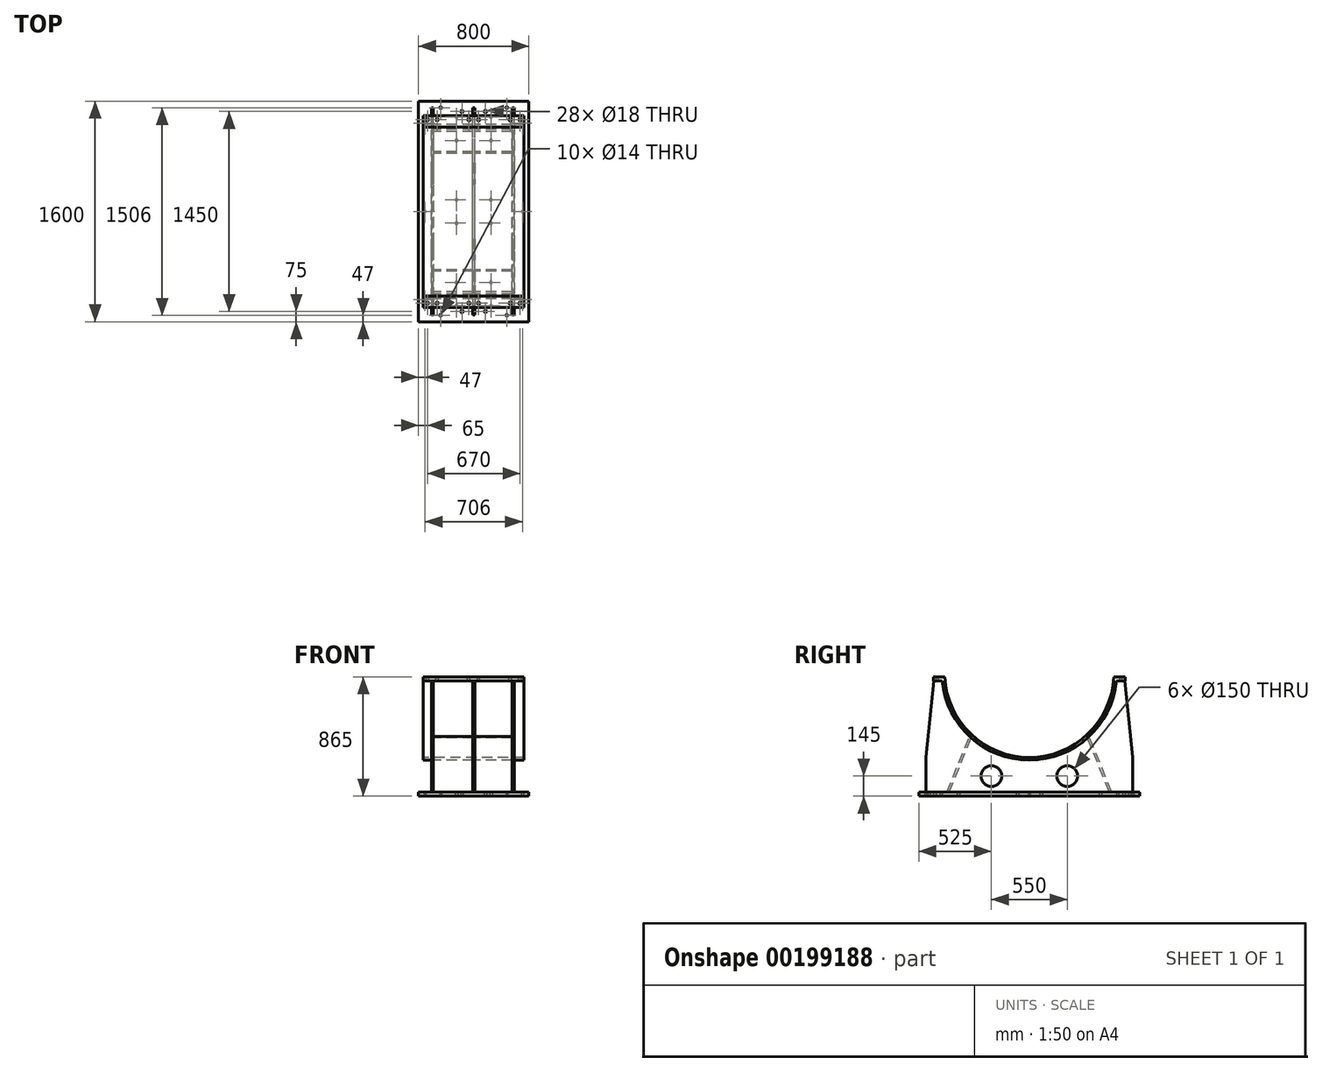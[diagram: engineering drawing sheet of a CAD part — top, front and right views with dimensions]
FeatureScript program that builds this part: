
annotation { "Feature Type Name" : "Feature", "Feature Type Description" : "" }
export const myFeature = defineFeature(function(context is Context, id is Id, definition is map)
    precondition{}
    {
        {
            var Q0;
            Q0=qCreatedBy(makeId("Right.planeOp"),FACE);
            var sketch = newSketch(context, id + "F0", { "sketchPlane" : qUnion([Q0])});
            skArc(sketch, "E0", {"start": v(-613.37, -30) * mm, "mid": v(0, -614.1) * mm, "end": v(613.37, -30) * mm});
            skArc(sketch, "E1", {"start": v(-633.39, -30) * mm, "mid": v(0, -634.1) * mm, "end": v(633.39, -30) * mm});
            skLineSegment(sketch, "E2", {"start": v(-634.1, 0) * mm, "end": v(634.1, 0) * mm, "construction": true});
            skLineSegment(sketch, "E3", {"start": v(-633.39, -30) * mm, "end": v(633.39, -30) * mm, "construction": true});
            skLineSegment(sketch, "E4", {"start": v(-633.39, -30) * mm, "end": v(-613.37, -30) * mm});
            skLineSegment(sketch, "E5", {"start": v(613.37, -30) * mm, "end": v(633.39, -30) * mm});
            skSolve(sketch);
        }
        {
            var Q0;
            Q0=makeQuery(id+"F0.imprint","IMPRINT",FACE,{"disambiguationData":[TD([[makeQuery(id+"F0.imprint","IMPRINT",EDGE,{"derivedFrom":sQuery(id+"F0.wireOp",EDGE,"E0")}),-1.0]])]});
            extrude(context, id + "F1", {"entities" : qUnion([Q0]), "endBound" : BoundingType.SYMMETRIC, "depth" : 730 * mm});
        }
        {
            var Q0;
            Q0=makeQuery(id+"F1.opExtrude","SWEPT_FACE",FACE,{"disambiguationData":[OSD([sQuery(id+"F0.wireOp",EDGE,"E5")])]});
            var sketch = newSketch(context, id + "F2", { "sketchPlane" : qUnion([Q0])});
            skLineSegment(sketch, "E6.bottom", {"start": v(-365, 613.37) * mm, "end": v(365, 613.37) * mm});
            skLineSegment(sketch, "E6.top", {"start": v(-365, 695.5) * mm, "end": v(365, 695.5) * mm});
            skLineSegment(sketch, "E6.left", {"start": v(-365, 613.37) * mm, "end": v(-365, 695.5) * mm});
            skLineSegment(sketch, "E6.right", {"start": v(365, 613.37) * mm, "end": v(365, 695.5) * mm});
            skLineSegment(sketch, "E7", {"start": v(-365, 0) * mm, "end": v(365, 0) * mm, "construction": true});
            skLineSegment(sketch, "E8.MirrorCS", {"start": v(-365, -613.37) * mm, "end": v(365, -613.37) * mm});
            skLineSegment(sketch, "E9.MirrorCS", {"start": v(-365, -613.37) * mm, "end": v(-365, -695.5) * mm});
            skLineSegment(sketch, "E10.MirrorCS", {"start": v(-365, -695.5) * mm, "end": v(365, -695.5) * mm});
            skLineSegment(sketch, "E11.MirrorCS", {"start": v(365, -613.37) * mm, "end": v(365, -695.5) * mm});
            skSolve(sketch);
        }
        {
            var Q0;
            Q0 = qSketchRegion(id + "F2", true);
            extrude(context, id + "F3", {"entities" : qUnion([Q0]), "operationType" : NewBodyOperationType.ADD, "oppositeDirection" : true, "depth" : 30 * mm});
        }
        {
            var Q0;
            Q0=makeQuery(id+"F3.boolean.opBoolean","MERGE",FACE,{"derivedFrom":[makeQuery(id+"F1.opExtrude","SWEPT_FACE",FACE,{"disambiguationData":[OSD([sQuery(id+"F0.wireOp",EDGE,"E5")])]}),makeQuery(id+"F3.opExtrude","CAP_FACE",FACE,{"disambiguationData":[OSD([sQuery(id+"F2.wireOp",EDGE,"E6.bottom"),sQuery(id+"F2.wireOp",EDGE,"E6.top"),sQuery(id+"F2.wireOp",EDGE,"E6.left"),sQuery(id+"F2.wireOp",EDGE,"E6.right")])],"isStart":true})]});
            var sketch = newSketch(context, id + "F4", { "sketchPlane" : qUnion([Q0])});
            skLineSegment(sketch, "E12", {"start": v(-365, 665.5) * mm, "end": v(365, 665.5) * mm, "construction": true});
            skCircle(sketch, "E13", {"center": v(-335, 665.5) * mm, "radius": 9 * mm});
            skCircle(sketch, "E14", {"center": v(-265, 665.5) * mm, "radius": 9 * mm});
            skCircle(sketch, "E15", {"center": v(-35, 665.5) * mm, "radius": 9 * mm});
            skCircle(sketch, "E16", {"center": v(35, 665.5) * mm, "radius": 9 * mm});
            skCircle(sketch, "E17", {"center": v(265, 665.5) * mm, "radius": 9 * mm});
            skCircle(sketch, "E18", {"center": v(335, 665.5) * mm, "radius": 9 * mm});
            skLineSegment(sketch, "E19", {"start": v(0, 0) * mm, "end": v(0, 665.5) * mm, "construction": true});
            skLineSegment(sketch, "E20", {"start": v(-365, 0) * mm, "end": v(365, 0) * mm, "construction": true});
            skCircle(sketch, "E21.MirrorC", {"center": v(-265, -665.5) * mm, "radius": 9 * mm});
            skCircle(sketch, "E22.MirrorC", {"center": v(-335, -665.5) * mm, "radius": 9 * mm});
            skCircle(sketch, "E23.MirrorC", {"center": v(-35, -665.5) * mm, "radius": 9 * mm});
            skCircle(sketch, "E24.MirrorC", {"center": v(35, -665.5) * mm, "radius": 9 * mm});
            skCircle(sketch, "E25.MirrorC", {"center": v(265, -665.5) * mm, "radius": 9 * mm});
            skCircle(sketch, "E26.MirrorC", {"center": v(335, -665.5) * mm, "radius": 9 * mm});
            skSolve(sketch);
        }
        {
            var Q0;
            Q0 = qSketchRegion(id + "F4", true);
            extrude(context, id + "F5", {"entities" : qUnion([Q0]), "operationType" : NewBodyOperationType.REMOVE, "endBound" : BoundingType.THROUGH_ALL, "oppositeDirection" : true, "depth" : 25 * mm});
        }
        {
            var Q0;
            Q0=makeQuery(id+"F3.boolean.opBoolean","MERGE",FACE,{"derivedFrom":[makeQuery(id+"F1.opExtrude","CAP_FACE",FACE,{"disambiguationData":[OSD([sQuery(id+"F0.wireOp",EDGE,"E0"),sQuery(id+"F0.wireOp",EDGE,"E1"),sQuery(id+"F0.wireOp",EDGE,"E4"),sQuery(id+"F0.wireOp",EDGE,"E5")])],"isStart":true}),makeQuery(id+"F3.opExtrude","SWEPT_FACE",FACE,{"disambiguationData":[OSD([sQuery(id+"F2.wireOp",EDGE,"E6.left")])]}),makeQuery(id+"F3.opExtrude","SWEPT_FACE",FACE,{"disambiguationData":[OSD([sQuery(id+"F2.wireOp",EDGE,"E9.MirrorCS")])]})]});
            cPlane(context, id + "F6", {"entities" : qUnion([Q0]), "cplaneType" : CPlaneType.OFFSET, "offset" : 73 * mm, "oppositeDirection" : true, "width" : 150 * mm, "height" : 150 * mm});
        }
        {
            var Q0;
            Q0=qCreatedBy(id+"F6.planeOp",FACE);
            var sketch = newSketch(context, id + "F7", { "sketchPlane" : qUnion([Q0])});
            skLineSegment(sketch, "E27", {"start": v(0, 0) * mm, "end": v(0, -865) * mm, "construction": true});
            skLineSegment(sketch, "E28", {"start": v(750, -865) * mm, "end": v(-750, -865) * mm});
            skLineSegment(sketch, "E29", {"start": v(-750, -865) * mm, "end": v(-750, -612) * mm});
            skLineSegment(sketch, "E30", {"start": v(-750, -612) * mm, "end": v(-692, -60) * mm});
            skLineSegment(sketch, "E31.0", {"start": v(-631.25, -60) * mm, "end": v(-692, -60) * mm});
            skPoint(sketch, "E32.orphan", {"position": v(-695.5, -60) * mm});
            skArc(sketch, "E33.0", {"start": v(631.25, -60) * mm, "mid": v(0, -634.1) * mm, "end": v(-631.25, -60) * mm});
            skLineSegment(sketch, "E34.MirrorCS", {"start": v(631.25, -60) * mm, "end": v(692, -60) * mm});
            skLineSegment(sketch, "E35.MirrorCS", {"start": v(750, -612) * mm, "end": v(692, -60) * mm});
            skLineSegment(sketch, "E36.MirrorCS", {"start": v(750, -865) * mm, "end": v(750, -612) * mm});
            skCircle(sketch, "E37", {"center": v(-275, -750) * mm, "radius": 75 * mm});
            skCircle(sketch, "E38.MirrorC", {"center": v(275, -750) * mm, "radius": 75 * mm});
            skSolve(sketch);
        }
        {
            var Q0;
            Q0=makeQuery(id+"F7.imprint","IMPRINT",FACE,{"disambiguationData":[TD([[makeQuery(id+"F7.imprint","IMPRINT",EDGE,{"derivedFrom":sQuery(id+"F7.wireOp",EDGE,"E28")}),-1.0]])]});
            extrude(context, id + "F8", {"entities" : qUnion([Q0]), "operationType" : NewBodyOperationType.ADD, "depth" : 15 * mm});
        }
        {
            var Q0;
            Q0=makeQuery(id+"F8.opExtrude","CAP_FACE",FACE,{"disambiguationData":[OSD([sQuery(id+"F7.wireOp",EDGE,"E28"),sQuery(id+"F7.wireOp",EDGE,"E29"),sQuery(id+"F7.wireOp",EDGE,"E30"),sQuery(id+"F7.wireOp",EDGE,"E31.0"),sQuery(id+"F7.wireOp",EDGE,"E33.0"),sQuery(id+"F7.wireOp",EDGE,"E34.MirrorCS"),sQuery(id+"F7.wireOp",EDGE,"E35.MirrorCS"),sQuery(id+"F7.wireOp",EDGE,"E36.MirrorCS"),sQuery(id+"F7.wireOp",EDGE,"E37"),sQuery(id+"F7.wireOp",EDGE,"E38.MirrorC")])],"isStart":true});
            cPlane(context, id + "F9", {"entities" : qUnion([Q0]), "cplaneType" : CPlaneType.OFFSET, "offset" : 300 * mm, "width" : 150 * mm, "height" : 150 * mm});
        }
        {
            var Q0;
            Q0=qCreatedBy(id+"F9.planeOp",FACE);
            var sketch = newSketch(context, id + "F10", { "sketchPlane" : qUnion([Q0])});
            skLineSegment(sketch, "E39.0", {"start": v(631.25, -60) * mm, "end": v(692, -60) * mm});
            skLineSegment(sketch, "E40.0", {"start": v(750, -612) * mm, "end": v(692, -60) * mm});
            skArc(sketch, "E41.0", {"start": v(-631.25, -60) * mm, "mid": v(0, -634.1) * mm, "end": v(631.25, -60) * mm});
            skLineSegment(sketch, "E42.0", {"start": v(750, -865) * mm, "end": v(750, -612) * mm});
            skLineSegment(sketch, "E43.0", {"start": v(-750, -865) * mm, "end": v(750, -865) * mm});
            skCircle(sketch, "E44.0", {"center": v(275, -750) * mm, "radius": 75 * mm});
            skCircle(sketch, "E45.0", {"center": v(-275, -750) * mm, "radius": 75 * mm});
            skLineSegment(sketch, "E46.0", {"start": v(-750, -865) * mm, "end": v(-750, -612) * mm});
            skLineSegment(sketch, "E47.0", {"start": v(-750, -612) * mm, "end": v(-692, -60) * mm});
            skLineSegment(sketch, "E48.0", {"start": v(-631.25, -60) * mm, "end": v(-692, -60) * mm});
            skSolve(sketch);
        }
        {
            var Q0;
            Q0=makeQuery(id+"F10.imprint","IMPRINT",FACE,{"disambiguationData":[TD([[makeQuery(id+"F10.imprint","IMPRINT",EDGE,{"derivedFrom":sQuery(id+"F10.wireOp",EDGE,"E39.0")}),-1.0]])]});
            extrude(context, id + "F11", {"entities" : qUnion([Q0]), "operationType" : NewBodyOperationType.ADD, "oppositeDirection" : true, "depth" : 15 * mm});
        }
        {
            var Q0;
            Q0=makeQuery(id+"F11.opExtrude","CAP_FACE",FACE,{"disambiguationData":[OSD([sQuery(id+"F10.wireOp",EDGE,"E39.0"),sQuery(id+"F10.wireOp",EDGE,"E40.0"),sQuery(id+"F10.wireOp",EDGE,"E41.0"),sQuery(id+"F10.wireOp",EDGE,"E42.0"),sQuery(id+"F10.wireOp",EDGE,"E43.0"),sQuery(id+"F10.wireOp",EDGE,"E44.0"),sQuery(id+"F10.wireOp",EDGE,"E45.0"),sQuery(id+"F10.wireOp",EDGE,"E46.0"),sQuery(id+"F10.wireOp",EDGE,"E47.0"),sQuery(id+"F10.wireOp",EDGE,"E48.0")])],"isStart":false});
            cPlane(context, id + "F12", {"entities" : qUnion([Q0]), "cplaneType" : CPlaneType.OFFSET, "offset" : 300 * mm, "oppositeDirection" : true, "width" : 150 * mm, "height" : 150 * mm});
        }
        {
            var Q0;
            Q0=qCreatedBy(id+"F12.planeOp",FACE);
            var sketch = newSketch(context, id + "F13", { "sketchPlane" : qUnion([Q0])});
            skLineSegment(sketch, "E49.0", {"start": v(750, -612) * mm, "end": v(692, -60) * mm});
            skLineSegment(sketch, "E50.0", {"start": v(750, -865) * mm, "end": v(750, -612) * mm});
            skLineSegment(sketch, "E51.0", {"start": v(750, -865) * mm, "end": v(-750, -865) * mm});
            skCircle(sketch, "E52.0", {"center": v(275, -750) * mm, "radius": 75 * mm});
            skCircle(sketch, "E53.0", {"center": v(-275, -750) * mm, "radius": 75 * mm});
            skLineSegment(sketch, "E54.0", {"start": v(-750, -865) * mm, "end": v(-750, -612) * mm});
            skLineSegment(sketch, "E55.0", {"start": v(-750, -612) * mm, "end": v(-692, -60) * mm});
            skArc(sketch, "E56.0", {"start": v(631.25, -60) * mm, "mid": v(0, -634.1) * mm, "end": v(-631.25, -60) * mm});
            skLineSegment(sketch, "E57.0", {"start": v(-631.25, -60) * mm, "end": v(-692, -60) * mm});
            skLineSegment(sketch, "E58.0", {"start": v(631.25, -60) * mm, "end": v(692, -60) * mm});
            skSolve(sketch);
        }
        {
            var Q0;
            Q0=makeQuery(id+"F13.imprint","IMPRINT",FACE,{"disambiguationData":[TD([[makeQuery(id+"F13.imprint","IMPRINT",EDGE,{"derivedFrom":sQuery(id+"F13.wireOp",EDGE,"E49.0")}),1.0]])]});
            extrude(context, id + "F14", {"entities" : qUnion([Q0]), "operationType" : NewBodyOperationType.ADD, "depth" : 15 * mm});
        }
        {
            var Q0;
            Q0=makeQuery(id+"F8.opExtrude","SWEPT_FACE",FACE,{"disambiguationData":[OSD([sQuery(id+"F7.wireOp",EDGE,"E28")])]});
            var sketch = newSketch(context, id + "F15", { "sketchPlane" : qUnion([Q0])});
            skLineSegment(sketch, "E59.bottom", {"start": v(-400, 800) * mm, "end": v(400, 800) * mm});
            skLineSegment(sketch, "E59.top", {"start": v(-400, -800) * mm, "end": v(400, -800) * mm});
            skLineSegment(sketch, "E59.left", {"start": v(-400, 800) * mm, "end": v(-400, -800) * mm});
            skLineSegment(sketch, "E59.right", {"start": v(400, 800) * mm, "end": v(400, -800) * mm});
            skLineSegment(sketch, "E60", {"start": v(0, 0) * mm, "end": v(400, 0) * mm, "construction": true});
            skLineSegment(sketch, "E61", {"start": v(0, 800) * mm, "end": v(0, 0) * mm, "construction": true});
            skSolve(sketch);
        }
        {
            var Q0;
            Q0 = qSketchRegion(id + "F15", true);
            extrude(context, id + "F16", {"entities" : qUnion([Q0]), "operationType" : NewBodyOperationType.ADD, "depth" : 30 * mm});
        }
        {
            var Q0;
            Q0=makeQuery(id+"F8.opExtrude","CAP_FACE",FACE,{"disambiguationData":[OSD([sQuery(id+"F7.wireOp",EDGE,"E28"),sQuery(id+"F7.wireOp",EDGE,"E29"),sQuery(id+"F7.wireOp",EDGE,"E30"),sQuery(id+"F7.wireOp",EDGE,"E31.0"),sQuery(id+"F7.wireOp",EDGE,"E33.0"),sQuery(id+"F7.wireOp",EDGE,"E34.MirrorCS"),sQuery(id+"F7.wireOp",EDGE,"E35.MirrorCS"),sQuery(id+"F7.wireOp",EDGE,"E36.MirrorCS"),sQuery(id+"F7.wireOp",EDGE,"E37"),sQuery(id+"F7.wireOp",EDGE,"E38.MirrorC")])],"isStart":false});
            var sketch = newSketch(context, id + "F17", { "sketchPlane" : qUnion([Q0])});
            skLineSegment(sketch, "E62", {"start": v(-596.7, -865) * mm, "end": v(-434, -462.3) * mm});
            skLineSegment(sketch, "E63", {"start": v(-580.52, -865) * mm, "end": v(-422.19, -473.12) * mm});
            skLineSegment(sketch, "E64", {"start": v(0, -865) * mm, "end": v(0, -634.1) * mm, "construction": true});
            skArc(sketch, "E65.0", {"start": v(631.25, -60) * mm, "mid": v(426.64, -469.11) * mm, "end": v(0, -634.1) * mm});
            skLineSegment(sketch, "E66.0", {"start": v(800, -865) * mm, "end": v(0, -865) * mm});
            skPoint(sketch, "E67.orphan", {"position": v(-631.25, -60) * mm});
            skArc(sketch, "E68.trimOffspring", {"start": v(-422.19, -473.12) * mm, "mid": v(-428.13, -467.75) * mm, "end": v(-434, -462.3) * mm});
            skLineSegment(sketch, "E69.trimOffspring", {"start": v(-580.52, -865) * mm, "end": v(-596.7, -865) * mm});
            skPoint(sketch, "E70.orphan", {"position": v(-800, -865) * mm});
            skLineSegment(sketch, "E71.MirrorCS", {"start": v(580.52, -865) * mm, "end": v(422.19, -473.12) * mm});
            skLineSegment(sketch, "E72.MirrorCS", {"start": v(596.7, -865) * mm, "end": v(434, -462.3) * mm});
            skArc(sketch, "E73.MirrorCS", {"start": v(422.19, -473.12) * mm, "mid": v(428.13, -467.75) * mm, "end": v(434, -462.3) * mm});
            skLineSegment(sketch, "E74.MirrorCS", {"start": v(580.52, -865) * mm, "end": v(596.7, -865) * mm});
            skSolve(sketch);
        }
        {
            var Q0;
            Q0 = qSketchRegion(id + "F17", true);
            var Q1;
            Q1=makeQuery(id+"F14.opExtrude","CAP_FACE",FACE,{"disambiguationData":[OSD([sQuery(id+"F13.wireOp",EDGE,"E49.0"),sQuery(id+"F13.wireOp",EDGE,"E50.0"),sQuery(id+"F13.wireOp",EDGE,"E51.0"),sQuery(id+"F13.wireOp",EDGE,"E52.0"),sQuery(id+"F13.wireOp",EDGE,"E53.0"),sQuery(id+"F13.wireOp",EDGE,"E54.0"),sQuery(id+"F13.wireOp",EDGE,"E55.0"),sQuery(id+"F13.wireOp",EDGE,"E56.0"),sQuery(id+"F13.wireOp",EDGE,"E57.0"),sQuery(id+"F13.wireOp",EDGE,"E58.0")])],"isStart":true});
            extrude(context, id + "F18", {"entities" : qUnion([Q0]), "operationType" : NewBodyOperationType.ADD, "endBound" : BoundingType.UP_TO_SURFACE, "oppositeDirection" : true, "endBoundEntityFace" : qUnion([Q1]), "depth" : 25 * mm});
        }
        {
            var Q0;
            Q0=makeQuery(id+"F16.opExtrude","CAP_FACE",FACE,{"disambiguationData":[OSD([sQuery(id+"F15.wireOp",EDGE,"E59.bottom"),sQuery(id+"F15.wireOp",EDGE,"E59.top"),sQuery(id+"F15.wireOp",EDGE,"E59.left"),sQuery(id+"F15.wireOp",EDGE,"E59.right")])],"isStart":false});
            var sketch = newSketch(context, id + "F19", { "sketchPlane" : qUnion([Q0])});
            skLineSegment(sketch, "E75", {"start": v(-400, 753) * mm, "end": v(400, 753) * mm, "construction": true});
            skLineSegment(sketch, "E76", {"start": v(-400, 725) * mm, "end": v(400, 725) * mm, "construction": true});
            skLineSegment(sketch, "E77", {"start": v(-400, 640) * mm, "end": v(400, 640) * mm, "construction": true});
            skLineSegment(sketch, "E78", {"start": v(-400, 0) * mm, "end": v(400, 0) * mm, "construction": true});
            skCircle(sketch, "E79", {"center": v(-353, 0) * mm, "radius": 7 * mm});
            skCircle(sketch, "E80", {"center": v(353, 0) * mm, "radius": 7 * mm});
            skCircle(sketch, "E81", {"center": v(-353, 640) * mm, "radius": 7 * mm});
            skLineSegment(sketch, "E82", {"start": v(0, 800) * mm, "end": v(0, 0) * mm, "construction": true});
            skCircle(sketch, "E83", {"center": v(-240, 753) * mm, "radius": 7 * mm});
            skCircle(sketch, "E84", {"center": v(-85, 725) * mm, "radius": 9 * mm});
            skCircle(sketch, "E85.MirrorC", {"center": v(85, 725) * mm, "radius": 9 * mm});
            skCircle(sketch, "E86.MirrorC", {"center": v(240, 753) * mm, "radius": 7 * mm});
            skCircle(sketch, "E87.MirrorC", {"center": v(353, 640) * mm, "radius": 7 * mm});
            skCircle(sketch, "E88.MirrorC", {"center": v(-353, -640) * mm, "radius": 7 * mm});
            skCircle(sketch, "E89.MirrorC", {"center": v(-240, -753) * mm, "radius": 7 * mm});
            skCircle(sketch, "E90.MirrorC", {"center": v(-85, -725) * mm, "radius": 9 * mm});
            skCircle(sketch, "E91.MirrorC", {"center": v(85, -725) * mm, "radius": 9 * mm});
            skCircle(sketch, "E92.MirrorC", {"center": v(353, -640) * mm, "radius": 7 * mm});
            skCircle(sketch, "E93.MirrorC", {"center": v(240, -753) * mm, "radius": 7 * mm});
            skSolve(sketch);
        }
        {
            var Q0;
            Q0 = qSketchRegion(id + "F19", true);
            extrude(context, id + "F20", {"entities" : qUnion([Q0]), "operationType" : NewBodyOperationType.REMOVE, "oppositeDirection" : true, "depth" : 31 * mm});
        }
        {
            var Q0;
            Q0=makeQuery(id+"F16.opExtrude","CAP_FACE",FACE,{"disambiguationData":[OSD([sQuery(id+"F15.wireOp",EDGE,"E59.bottom"),sQuery(id+"F15.wireOp",EDGE,"E59.top"),sQuery(id+"F15.wireOp",EDGE,"E59.left"),sQuery(id+"F15.wireOp",EDGE,"E59.right")])],"isStart":false});
            var sketch = newSketch(context, id + "F21", { "sketchPlane" : qUnion([Q0])});
            skLineSegment(sketch, "E94", {"start": v(400, 700) * mm, "end": v(-400, 700) * mm, "construction": true});
            skLineSegment(sketch, "E95", {"start": v(-400, 500) * mm, "end": v(400, 500) * mm, "construction": true});
            skLineSegment(sketch, "E96", {"start": v(-400, 100) * mm, "end": v(400, 100) * mm, "construction": true});
            skLineSegment(sketch, "E97", {"start": v(-400, -100) * mm, "end": v(400, -100) * mm, "construction": true});
            skLineSegment(sketch, "E98", {"start": v(-400, -400) * mm, "end": v(400, -400) * mm, "construction": true});
            skLineSegment(sketch, "E99", {"start": v(-400, -600) * mm, "end": v(400, -600) * mm, "construction": true});
            skLineSegment(sketch, "E100", {"start": v(-400, 0) * mm, "end": v(400, 0) * mm, "construction": true});
            skLineSegment(sketch, "E101", {"start": v(-400, 600) * mm, "end": v(400, 600) * mm, "construction": true});
            skLineSegment(sketch, "E102", {"start": v(0, 800) * mm, "end": v(0, 0) * mm, "construction": true});
            skCircle(sketch, "E103", {"center": v(-125, 685) * mm, "radius": 9 * mm});
            skCircle(sketch, "E104", {"center": v(-125, 515) * mm, "radius": 9 * mm});
            skCircle(sketch, "E105.MirrorC", {"center": v(125, 685) * mm, "radius": 9 * mm});
            skCircle(sketch, "E106.MirrorC", {"center": v(125, 515) * mm, "radius": 9 * mm});
            skCircle(sketch, "E107", {"center": v(-125, 85) * mm, "radius": 9 * mm});
            skCircle(sketch, "E108.MirrorC", {"center": v(125, 85) * mm, "radius": 9 * mm});
            skCircle(sketch, "E109.MirrorC", {"center": v(-125, -85) * mm, "radius": 9 * mm});
            skCircle(sketch, "E110.MirrorC", {"center": v(125, -85) * mm, "radius": 9 * mm});
            skCircle(sketch, "E111.MirrorC", {"center": v(-125, -685) * mm, "radius": 9 * mm});
            skCircle(sketch, "E112.MirrorC", {"center": v(125, -685) * mm, "radius": 9 * mm});
            skCircle(sketch, "E113.MirrorC", {"center": v(125, -515) * mm, "radius": 9 * mm});
            skCircle(sketch, "E114.MirrorC", {"center": v(-125, -515) * mm, "radius": 9 * mm});
            skSolve(sketch);
        }
        {
            var Q0;
            Q0 = qSketchRegion(id + "F21", true);
            extrude(context, id + "F22", {"entities" : qUnion([Q0]), "operationType" : NewBodyOperationType.REMOVE, "oppositeDirection" : true, "depth" : 31 * mm});
        }
    });
